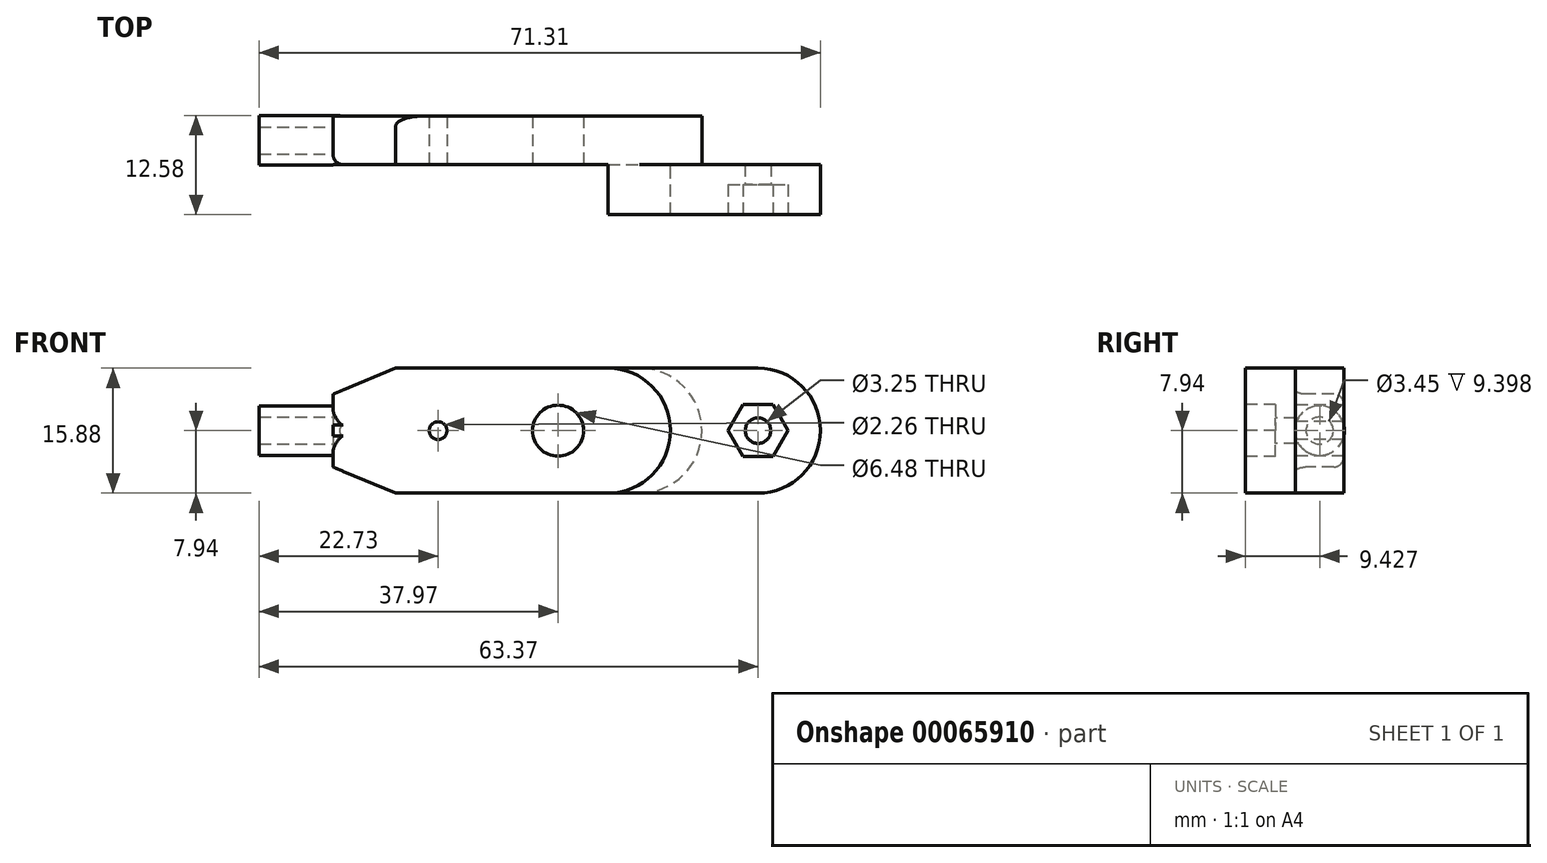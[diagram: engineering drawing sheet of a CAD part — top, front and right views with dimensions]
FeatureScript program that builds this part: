
annotation { "Feature Type Name" : "Feature", "Feature Type Description" : "" }
export const myFeature = defineFeature(function(context is Context, id is Id, definition is map)
    precondition{}
    {
        {
            var Q0;
            Q0=qCreatedBy(makeId("Front.planeOp"),FACE);
            var sketch = newSketch(context, id + "F0", { "sketchPlane" : qUnion([Q0])});
            skLineSegment(sketch, "E0.rect.bottom", {"start": v(34.92, 7.94) * mm, "end": v(-34.92, 7.94) * mm});
            skLineSegment(sketch, "E0.rect.top", {"start": v(34.92, -7.94) * mm, "end": v(-34.92, -7.94) * mm});
            skLineSegment(sketch, "E0.rect.left", {"start": v(34.93, 7.94) * mm, "end": v(34.93, -7.94) * mm});
            skLineSegment(sketch, "E0.rect.right", {"start": v(-34.93, 7.94) * mm, "end": v(-34.93, -7.94) * mm});
            skPoint(sketch, "E0.rect.middle", {"position": v(0, 0) * mm});
            skSolve(sketch);
        }
        {
            var Q0;
            Q0 = qSketchRegion(id + "F0", true);
            extrude(context, id + "F1", {"entities" : qUnion([Q0]), "depth" : 6.15 * mm});
        }
        {
            var Q0;
            Q0=makeQuery(id+"F1.opExtrude","CAP_FACE",FACE,{"disambiguationData":[OSD([sQuery(id+"F0.wireOp",EDGE,"E0.rect.bottom"),sQuery(id+"F0.wireOp",EDGE,"E0.rect.top"),sQuery(id+"F0.wireOp",EDGE,"E0.rect.left"),sQuery(id+"F0.wireOp",EDGE,"E0.rect.right")])],"isStart":false});
            var sketch = newSketch(context, id + "F2", { "sketchPlane" : qUnion([Q0])});
            skCircle(sketch, "E1", {"center": v(-6.35, 0) * mm, "radius": 3.24 * mm});
            skCircle(sketch, "E2", {"center": v(-21.59, 0) * mm, "radius": 1.13 * mm});
            skSolve(sketch);
        }
        {
            var Q0;
            Q0 = qSketchRegion(id + "F2", true);
            extrude(context, id + "F3", {"entities" : qUnion([Q0]), "operationType" : NewBodyOperationType.REMOVE, "endBound" : BoundingType.THROUGH_ALL, "oppositeDirection" : true, "depth" : 25.4 * mm});
        }
        {
            var Q0;
            Q0=makeQuery(id+"F1.opExtrude","SWEPT_FACE",FACE,{"disambiguationData":[OSD([sQuery(id+"F0.wireOp",EDGE,"E0.rect.right")])]});
            var sketch = newSketch(context, id + "F4", { "sketchPlane" : qUnion([Q0])});
            skCircle(sketch, "E3", {"center": v(3.07, 0) * mm, "radius": 3.15 * mm});
            skPoint(sketch, "E3.centerSnap0", {"position": v(6.15, 0) * mm});
            skLineSegment(sketch, "E4", {"start": v(3.07, 0) * mm, "end": v(3.07, -7.94) * mm, "construction": true});
            skLineSegment(sketch, "E5", {"start": v(3.07, 0) * mm, "end": v(6.15, 0) * mm, "construction": true});
            skCircle(sketch, "E6", {"center": v(3.07, 0) * mm, "radius": 1.73 * mm});
            skSolve(sketch);
        }
        {
            var Q0;
            Q0 = qSketchRegion(id + "F4", true);
            extrude(context, id + "F5", {"entities" : qUnion([Q0]), "operationType" : NewBodyOperationType.ADD, "depth" : 9.4 * mm});
        }
        {
            var Q0;
            Q0=makeQuery(id+"F1.opExtrude","SWEPT_FACE",FACE,{"disambiguationData":[OSD([sQuery(id+"F0.wireOp",EDGE,"E0.rect.left")])]});
            var sketch = newSketch(context, id + "F6", { "sketchPlane" : qUnion([Q0])});
            skCircle(sketch, "E7", {"center": v(-3.07, 4.76) * mm, "radius": 1.13 * mm});
            skCircle(sketch, "E8", {"center": v(-3.07, -4.76) * mm, "radius": 1.13 * mm});
            skLineSegment(sketch, "E9", {"start": v(-3.07, 4.76) * mm, "end": v(-3.07, -4.76) * mm, "construction": true});
            skLineSegment(sketch, "E10", {"start": v(0, 0) * mm, "end": v(-3.07, 0) * mm, "construction": true});
            skLineSegment(sketch, "E11", {"start": v(-3.07, -4.76) * mm, "end": v(-3.07, -7.94) * mm, "construction": true});
            skSolve(sketch);
        }
        {
            var Q0;
            {var subQ0=sQuery(id+"F0.wireOp",EDGE,"E0.rect.right");Q0=makeQuery(id+"F5.boolean.opBoolean","SPLIT",EDGE,{"disambiguationData":[topologyDisambiguationEdgeConnected([makeQuery(id+"F1.opExtrude","CAP_FACE",FACE,{"disambiguationData":[OSD([sQuery(id+"F0.wireOp",EDGE,"E0.rect.bottom"),sQuery(id+"F0.wireOp",EDGE,"E0.rect.top"),sQuery(id+"F0.wireOp",EDGE,"E0.rect.left"),subQ0])],"isStart":true}),makeQuery(id+"F5.opExtrude","CAP_FACE",FACE,{"disambiguationData":[OSD([sQuery(id+"F4.wireOp",EDGE,"E3"),sQuery(id+"F4.wireOp",EDGE,"E6")])],"isStart":true})])],"derivedFrom":makeQuery(id+"F1.opExtrude","CAP_EDGE",EDGE,{"disambiguationData":[OSD([subQ0])],"isStart":true})});}
            var Q1;
            {var subQ0=sQuery(id+"F0.wireOp",EDGE,"E0.rect.right");Q1=makeQuery(id+"F5.boolean.opBoolean","SPLIT",EDGE,{"disambiguationData":[topologyDisambiguationEdgeConnected([makeQuery(id+"F1.opExtrude","CAP_FACE",FACE,{"disambiguationData":[OSD([sQuery(id+"F0.wireOp",EDGE,"E0.rect.bottom"),sQuery(id+"F0.wireOp",EDGE,"E0.rect.top"),sQuery(id+"F0.wireOp",EDGE,"E0.rect.left"),subQ0])],"isStart":false}),makeQuery(id+"F5.opExtrude","CAP_FACE",FACE,{"disambiguationData":[OSD([sQuery(id+"F4.wireOp",EDGE,"E3"),sQuery(id+"F4.wireOp",EDGE,"E6")])],"isStart":true})])],"derivedFrom":makeQuery(id+"F1.opExtrude","CAP_EDGE",EDGE,{"disambiguationData":[OSD([subQ0])],"isStart":false})});}
            fillet(context, id + "F7", {"entities" : qUnion([Q0, Q1]), "radius" : 1.27 * mm, "tangentPropagation" : true, "allowEdgeOverflow" : false});
        }
        {
            var Q0;
            Q0=makeQuery(id+"F1.opExtrude","CAP_FACE",FACE,{"disambiguationData":[OSD([sQuery(id+"F0.wireOp",EDGE,"E0.rect.bottom"),sQuery(id+"F0.wireOp",EDGE,"E0.rect.top"),sQuery(id+"F0.wireOp",EDGE,"E0.rect.left"),sQuery(id+"F0.wireOp",EDGE,"E0.rect.right")])],"isStart":false});
            var sketch = newSketch(context, id + "F8", { "sketchPlane" : qUnion([Q0])});
            skLineSegment(sketch, "E12", {"start": v(-26.97, 7.94) * mm, "end": v(-34.93, 4.64) * mm});
            skLineSegment(sketch, "E13", {"start": v(-34.93, 4.64) * mm, "end": v(-34.93, 7.94) * mm});
            skLineSegment(sketch, "E14", {"start": v(-34.93, 7.94) * mm, "end": v(-26.97, 7.94) * mm});
            skLineSegment(sketch, "E15", {"start": v(-26.97, -7.94) * mm, "end": v(-34.93, -7.94) * mm});
            skLineSegment(sketch, "E16", {"start": v(-34.93, -7.94) * mm, "end": v(-34.93, -4.64) * mm});
            skLineSegment(sketch, "E17", {"start": v(-34.93, -4.64) * mm, "end": v(-26.97, -7.94) * mm});
            skSolve(sketch);
        }
        {
            var Q0;
            Q0 = qSketchRegion(id + "F8", true);
            extrude(context, id + "F9", {"entities" : qUnion([Q0]), "operationType" : NewBodyOperationType.REMOVE, "oppositeDirection" : true, "depth" : 25.4 * mm});
        }
        {
            var Q0;
            Q0=makeQuery(id+"F1.opExtrude","CAP_FACE",FACE,{"disambiguationData":[OSD([sQuery(id+"F0.wireOp",EDGE,"E0.rect.bottom"),sQuery(id+"F0.wireOp",EDGE,"E0.rect.top"),sQuery(id+"F0.wireOp",EDGE,"E0.rect.left"),sQuery(id+"F0.wireOp",EDGE,"E0.rect.right")])],"isStart":false});
            var sketch = newSketch(context, id + "F10", { "sketchPlane" : qUnion([Q0])});
            skArc(sketch, "E18", {"start": v(3.98, -7.94) * mm, "mid": v(11.91, 0) * mm, "end": v(3.98, 7.94) * mm});
            skLineSegment(sketch, "E19", {"start": v(3.98, 7.94) * mm, "end": v(34.93, 7.94) * mm});
            skLineSegment(sketch, "E20", {"start": v(34.93, 7.94) * mm, "end": v(34.93, -7.94) * mm});
            skLineSegment(sketch, "E21", {"start": v(34.93, -7.94) * mm, "end": v(3.98, -7.94) * mm});
            skSolve(sketch);
        }
        {
            var Q0;
            Q0 = qSketchRegion(id + "F10", true);
            extrude(context, id + "F11", {"entities" : qUnion([Q0]), "operationType" : NewBodyOperationType.REMOVE, "oppositeDirection" : true, "depth" : 25.4 * mm});
        }
        {
            var Q0;
            Q0=makeQuery(id+"F1.opExtrude","CAP_FACE",FACE,{"disambiguationData":[OSD([sQuery(id+"F0.wireOp",EDGE,"E0.rect.bottom"),sQuery(id+"F0.wireOp",EDGE,"E0.rect.top"),sQuery(id+"F0.wireOp",EDGE,"E0.rect.left"),sQuery(id+"F0.wireOp",EDGE,"E0.rect.right")])],"isStart":false});
            var sketch = newSketch(context, id + "F12", { "sketchPlane" : qUnion([Q0])});
            skArc(sketch, "E22", {"start": v(0, -7.94) * mm, "mid": v(7.94, 0) * mm, "end": v(0, 7.94) * mm});
            skLineSegment(sketch, "E23", {"start": v(0, 7.94) * mm, "end": v(19.05, 7.94) * mm});
            skLineSegment(sketch, "E24", {"start": v(0, -7.94) * mm, "end": v(19.05, -7.94) * mm});
            skArc(sketch, "E25", {"start": v(19.05, -7.94) * mm, "mid": v(26.99, 0) * mm, "end": v(19.05, 7.94) * mm});
            skSolve(sketch);
        }
        {
            var Q0;
            Q0 = qSketchRegion(id + "F12", true);
            extrude(context, id + "F13", {"entities" : qUnion([Q0]), "operationType" : NewBodyOperationType.ADD, "depth" : 6.35 * mm});
        }
        {
            var Q0;
            Q0=makeQuery(id+"F13.opExtrude","CAP_FACE",FACE,{"disambiguationData":[OSD([sQuery(id+"F12.wireOp",EDGE,"E22"),sQuery(id+"F12.wireOp",EDGE,"E23"),sQuery(id+"F12.wireOp",EDGE,"E24"),sQuery(id+"F12.wireOp",EDGE,"E25")])],"isStart":false});
            var sketch = newSketch(context, id + "F14", { "sketchPlane" : qUnion([Q0])});
            skCircle(sketch, "E26", {"center": v(19.05, 0) * mm, "radius": 1.63 * mm});
            skSolve(sketch);
        }
        {
            var Q0;
            Q0 = qSketchRegion(id + "F14", true);
            extrude(context, id + "F15", {"entities" : qUnion([Q0]), "operationType" : NewBodyOperationType.REMOVE, "oppositeDirection" : true, "depth" : 25.4 * mm});
        }
        {
            var Q0;
            Q0=makeQuery(id+"F13.opExtrude","CAP_FACE",FACE,{"disambiguationData":[OSD([sQuery(id+"F12.wireOp",EDGE,"E22"),sQuery(id+"F12.wireOp",EDGE,"E23"),sQuery(id+"F12.wireOp",EDGE,"E24"),sQuery(id+"F12.wireOp",EDGE,"E25")])],"isStart":false});
            var sketch = newSketch(context, id + "F16", { "sketchPlane" : qUnion([Q0])});
            skCircle(sketch, "E27.cCircle", {"center": v(19.05, 0) * mm, "radius": 3.3 * mm, "construction": true});
            skLineSegment(sketch, "E27.0", {"start": v(20.96, 3.3) * mm, "end": v(22.86, 0) * mm});
            skLineSegment(sketch, "E27.1", {"start": v(22.86, 0) * mm, "end": v(20.96, -3.3) * mm});
            skLineSegment(sketch, "E27.2", {"start": v(20.96, -3.3) * mm, "end": v(17.14, -3.3) * mm});
            skLineSegment(sketch, "E27.3", {"start": v(17.14, -3.3) * mm, "end": v(15.24, 0) * mm});
            skLineSegment(sketch, "E27.4", {"start": v(15.24, 0) * mm, "end": v(17.14, 3.3) * mm});
            skLineSegment(sketch, "E27.5", {"start": v(17.14, 3.3) * mm, "end": v(20.96, 3.3) * mm});
            skPoint(sketch, "E27.0.midPoint", {"position": v(21.9, 1.65) * mm});
            skSolve(sketch);
        }
        {
            var Q0;
            Q0 = qSketchRegion(id + "F16", true);
            extrude(context, id + "F17", {"entities" : qUnion([Q0]), "operationType" : NewBodyOperationType.REMOVE, "oppositeDirection" : true, "depth" : 3.8 * mm});
        }
        {
            var Q0;
            Q0=makeQuery(id+"F9.boolean.opBoolean","COPY",EDGE,{"derivedFrom":makeQuery(id+"F9.opExtrude","CAP_EDGE",EDGE,{"disambiguationData":[OSD([sQuery(id+"F8.wireOp",EDGE,"E17")])],"isStart":true})});
            var Q1;
            Q1=makeQuery(id+"F9.boolean.opBoolean","INTERSECT",EDGE,{"derivedFrom":[makeQuery(id+"F1.opExtrude","CAP_FACE",FACE,{"disambiguationData":[OSD([sQuery(id+"F0.wireOp",EDGE,"E0.rect.bottom"),sQuery(id+"F0.wireOp",EDGE,"E0.rect.top"),sQuery(id+"F0.wireOp",EDGE,"E0.rect.left"),sQuery(id+"F0.wireOp",EDGE,"E0.rect.right")])],"isStart":true}),makeQuery(id+"F9.opExtrude","SWEPT_FACE",FACE,{"disambiguationData":[OSD([sQuery(id+"F8.wireOp",EDGE,"E17")])]})]});
            var Q2;
            Q2=makeQuery(id+"F9.boolean.opBoolean","INTERSECT",EDGE,{"derivedFrom":[makeQuery(id+"F1.opExtrude","CAP_FACE",FACE,{"disambiguationData":[OSD([sQuery(id+"F0.wireOp",EDGE,"E0.rect.bottom"),sQuery(id+"F0.wireOp",EDGE,"E0.rect.top"),sQuery(id+"F0.wireOp",EDGE,"E0.rect.left"),sQuery(id+"F0.wireOp",EDGE,"E0.rect.right")])],"isStart":true}),makeQuery(id+"F9.opExtrude","SWEPT_FACE",FACE,{"disambiguationData":[OSD([sQuery(id+"F8.wireOp",EDGE,"E12")])]})]});
            var Q3;
            Q3=makeQuery(id+"F9.boolean.opBoolean","COPY",EDGE,{"derivedFrom":makeQuery(id+"F9.opExtrude","CAP_EDGE",EDGE,{"disambiguationData":[OSD([sQuery(id+"F8.wireOp",EDGE,"E12")])],"isStart":true})});
            fillet(context, id + "F18", {"entities" : qUnion([Q0, Q1, Q2, Q3]), "radius" : 1.27 * mm, "tangentPropagation" : true, "allowEdgeOverflow" : false});
        }
    });
